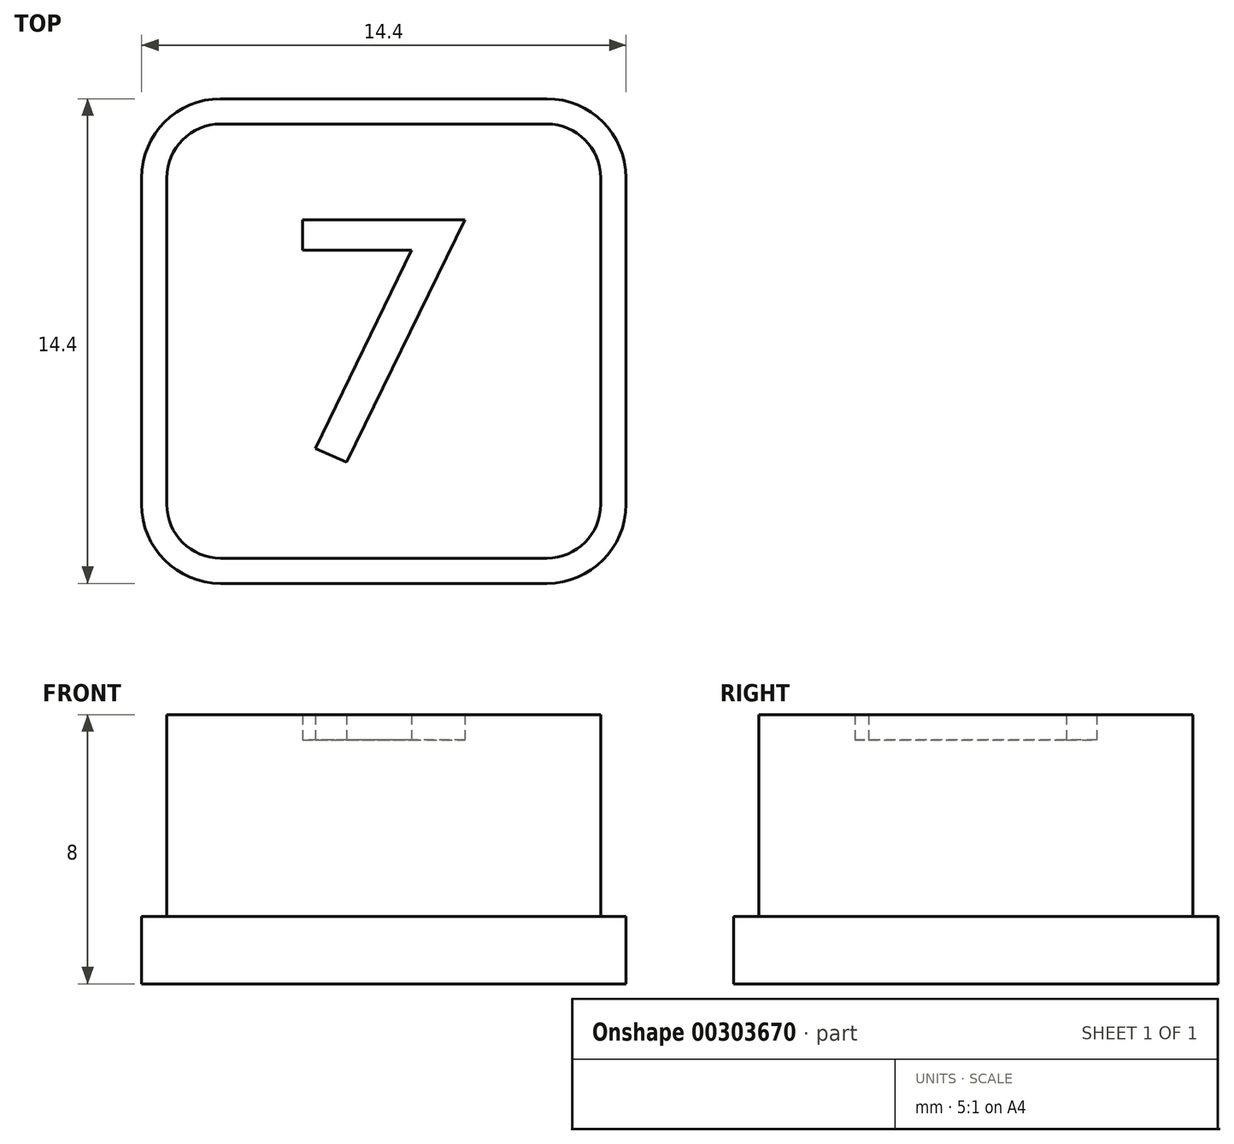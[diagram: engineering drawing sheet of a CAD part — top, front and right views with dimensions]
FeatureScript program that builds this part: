
annotation { "Feature Type Name" : "Feature", "Feature Type Description" : "" }
export const myFeature = defineFeature(function(context is Context, id is Id, definition is map)
    precondition{}
    {
        {
            var Q0;
            Q0=qCreatedBy(makeId("Top.planeOp"),FACE);
            var sketch = newSketch(context, id + "F0", { "sketchPlane" : qUnion([Q0])});
            skArc(sketch, "E0", {"start": v(4.85, -6.45) * mm, "mid": v(5.98, -5.98) * mm, "end": v(6.45, -4.85) * mm});
            skLineSegment(sketch, "E1", {"start": v(6.45, -4.85) * mm, "end": v(6.45, 4.85) * mm});
            skArc(sketch, "E2", {"start": v(6.45, 4.85) * mm, "mid": v(5.98, 5.98) * mm, "end": v(4.85, 6.45) * mm});
            skLineSegment(sketch, "E3", {"start": v(4.85, 6.45) * mm, "end": v(-4.85, 6.45) * mm});
            skArc(sketch, "E4", {"start": v(-4.85, 6.45) * mm, "mid": v(-5.98, 5.98) * mm, "end": v(-6.45, 4.85) * mm});
            skLineSegment(sketch, "E5", {"start": v(-6.45, 4.85) * mm, "end": v(-6.45, -4.85) * mm});
            skArc(sketch, "E6", {"start": v(-6.45, -4.85) * mm, "mid": v(-5.98, -5.98) * mm, "end": v(-4.85, -6.45) * mm});
            skLineSegment(sketch, "E7", {"start": v(-4.85, -6.45) * mm, "end": v(4.85, -6.45) * mm});
            skArc(sketch, "E8", {"start": v(-4.85, 7.2) * mm, "mid": v(-6.51, 6.51) * mm, "end": v(-7.2, 4.85) * mm});
            skLineSegment(sketch, "E9", {"start": v(-7.2, 4.85) * mm, "end": v(-7.2, -4.85) * mm});
            skArc(sketch, "E10", {"start": v(-7.2, -4.85) * mm, "mid": v(-6.51, -6.51) * mm, "end": v(-4.85, -7.2) * mm});
            skLineSegment(sketch, "E11", {"start": v(-4.85, -7.2) * mm, "end": v(4.85, -7.2) * mm});
            skArc(sketch, "E12", {"start": v(4.85, -7.2) * mm, "mid": v(6.51, -6.51) * mm, "end": v(7.2, -4.85) * mm});
            skLineSegment(sketch, "E13", {"start": v(7.2, -4.85) * mm, "end": v(7.2, 4.85) * mm});
            skArc(sketch, "E14", {"start": v(7.2, 4.85) * mm, "mid": v(6.51, 6.51) * mm, "end": v(4.85, 7.2) * mm});
            skLineSegment(sketch, "E15", {"start": v(4.85, 7.2) * mm, "end": v(-4.85, 7.2) * mm});
            skLineSegment(sketch, "E16", {"start": v(-2.03, -3.19) * mm, "end": v(0.82, 2.7) * mm});
            skLineSegment(sketch, "E17", {"start": v(0.82, 2.7) * mm, "end": v(-2.41, 2.7) * mm});
            skLineSegment(sketch, "E18", {"start": v(-2.41, 2.7) * mm, "end": v(-2.41, 3.6) * mm});
            skLineSegment(sketch, "E19", {"start": v(-2.41, 3.6) * mm, "end": v(2.41, 3.6) * mm});
            skLineSegment(sketch, "E20", {"start": v(2.41, 3.6) * mm, "end": v(-1.11, -3.6) * mm});
            skLineSegment(sketch, "E21", {"start": v(-1.11, -3.6) * mm, "end": v(-2.03, -3.19) * mm});
            skSolve(sketch);
        }
        {
            var Q0;
            Q0=makeQuery(id+"F0.imprint","IMPRINT",FACE,{"disambiguationData":[TD([[makeQuery(id+"F0.imprint","IMPRINT",EDGE,{"derivedFrom":sQuery(id+"F0.wireOp",EDGE,"E0")}),-1.0]])]});
            extrude(context, id + "F1", {"entities" : qUnion([Q0]), "depth" : 2 * mm});
        }
        {
            var Q0;
            Q0=makeQuery(id+"F0.imprint","IMPRINT",FACE,{"disambiguationData":[TD([[makeQuery(id+"F0.imprint","IMPRINT",EDGE,{"derivedFrom":sQuery(id+"F0.wireOp",EDGE,"E0")}),1.0]])]});
            extrude(context, id + "F2", {"entities" : qUnion([Q0]), "operationType" : NewBodyOperationType.ADD, "depth" : 8 * mm});
        }
        {
            var Q0;
            Q0=makeQuery(id+"F0.imprint","IMPRINT",FACE,{"disambiguationData":[TD([[makeQuery(id+"F0.imprint","IMPRINT",EDGE,{"derivedFrom":sQuery(id+"F0.wireOp",EDGE,"E16")}),-1.0]])]});
            extrude(context, id + "F3", {"entities" : qUnion([Q0]), "operationType" : NewBodyOperationType.ADD, "depth" : 7.25 * mm});
        }
    });
